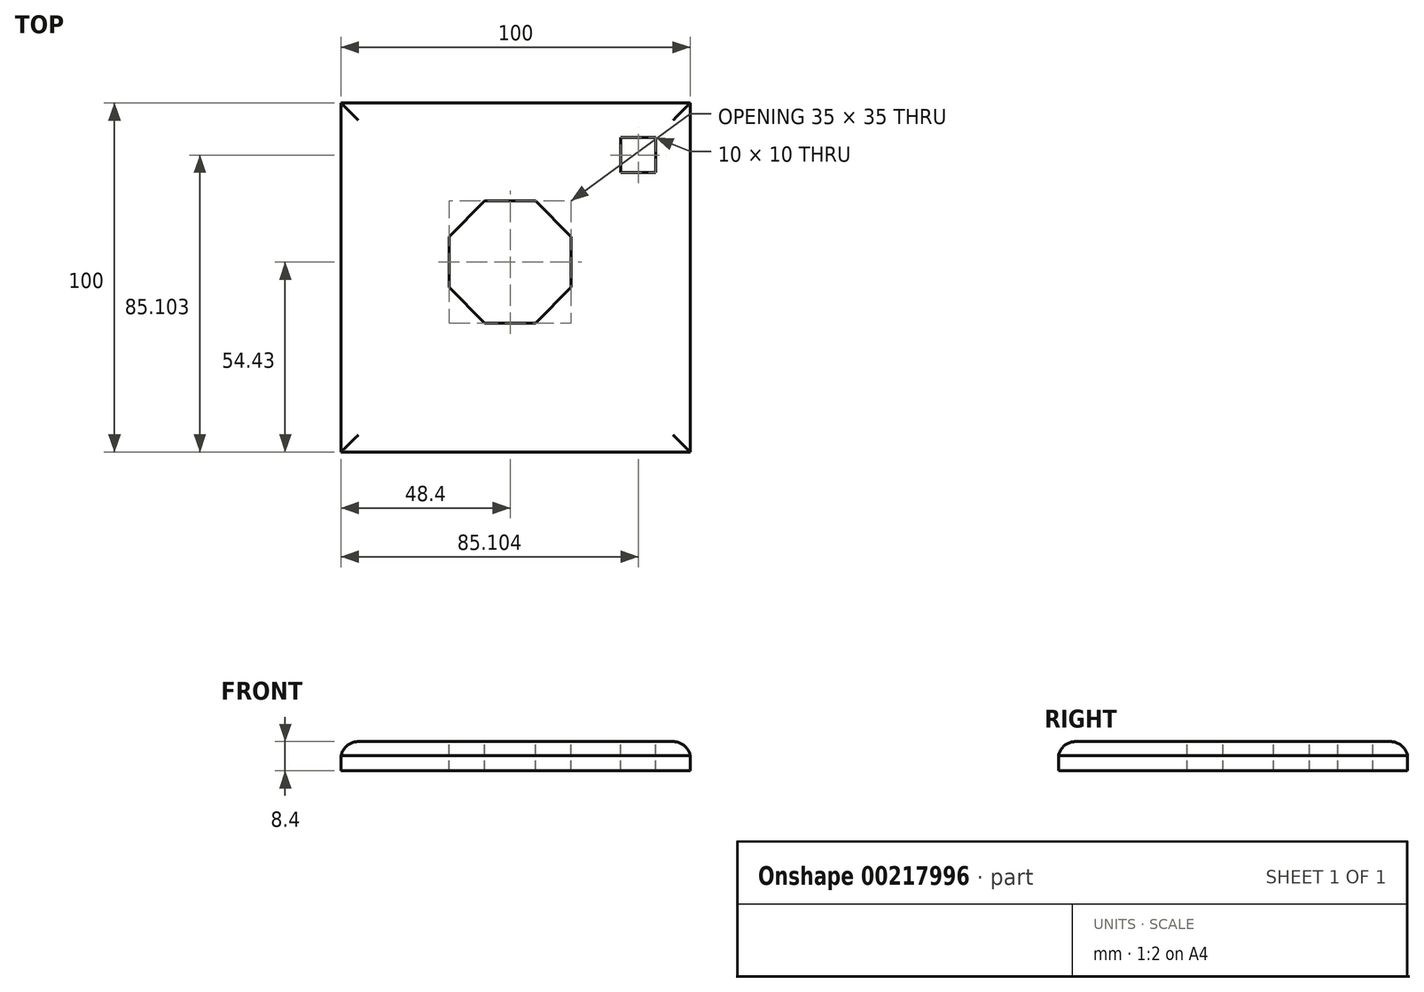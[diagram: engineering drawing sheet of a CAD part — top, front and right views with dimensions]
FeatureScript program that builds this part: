
annotation { "Feature Type Name" : "Feature", "Feature Type Description" : "" }
export const myFeature = defineFeature(function(context is Context, id is Id, definition is map)
    precondition{}
    {
        {
            var Q0;
            Q0=qCreatedBy(makeId("Top.planeOp"),FACE);
            var sketch = newSketch(context, id + "F0", { "sketchPlane" : qUnion([Q0])});
            skLineSegment(sketch, "E0.bottom", {"start": v(-48.4, 45.57) * mm, "end": v(51.6, 45.57) * mm});
            skLineSegment(sketch, "E0.top", {"start": v(-48.4, -54.43) * mm, "end": v(51.6, -54.43) * mm});
            skLineSegment(sketch, "E0.left", {"start": v(-48.4, 45.57) * mm, "end": v(-48.4, -54.43) * mm});
            skLineSegment(sketch, "E0.right", {"start": v(51.6, 45.57) * mm, "end": v(51.6, -54.43) * mm});
            skSolve(sketch);
        }
        {
            var Q0;
            Q0=makeQuery(id+"F0.imprint","IMPRINT",FACE,{"disambiguationData":[TD([[makeQuery(id+"F0.imprint","IMPRINT",EDGE,{"derivedFrom":sQuery(id+"F0.wireOp",EDGE,"E0.bottom")}),-1.0]])]});
            extrude(context, id + "F1", {"entities" : qUnion([Q0]), "depth" : 4 * mm});
        }
        {
            var Q0;
            Q0=makeQuery(id+"F1.opExtrude","CAP_FACE",FACE,{"disambiguationData":[OSD([sQuery(id+"F0.wireOp",EDGE,"E0.bottom"),sQuery(id+"F0.wireOp",EDGE,"E0.top"),sQuery(id+"F0.wireOp",EDGE,"E0.left"),sQuery(id+"F0.wireOp",EDGE,"E0.right")])],"isStart":false});
            var sketch = newSketch(context, id + "F2", { "sketchPlane" : qUnion([Q0])});
            skCircle(sketch, "E1.cCircle", {"center": v(0, 0) * mm, "radius": 17.5 * mm, "construction": true});
            skLineSegment(sketch, "E1.0", {"start": v(7.25, -17.5) * mm, "end": v(-7.25, -17.5) * mm});
            skLineSegment(sketch, "E1.1", {"start": v(-7.25, -17.5) * mm, "end": v(-17.5, -7.25) * mm});
            skLineSegment(sketch, "E1.2", {"start": v(-17.5, -7.25) * mm, "end": v(-17.5, 7.25) * mm});
            skLineSegment(sketch, "E1.3", {"start": v(-17.5, 7.25) * mm, "end": v(-7.25, 17.5) * mm});
            skLineSegment(sketch, "E1.4", {"start": v(-7.25, 17.5) * mm, "end": v(7.25, 17.5) * mm});
            skLineSegment(sketch, "E1.5", {"start": v(7.25, 17.5) * mm, "end": v(17.5, 7.25) * mm});
            skLineSegment(sketch, "E1.6", {"start": v(17.5, 7.25) * mm, "end": v(17.5, -7.25) * mm});
            skLineSegment(sketch, "E1.7", {"start": v(17.5, -7.25) * mm, "end": v(7.25, -17.5) * mm});
            skPoint(sketch, "E1.0.midPoint", {"position": v(0, -17.5) * mm});
            skSolve(sketch);
        }
        {
            var Q0;
            Q0=makeQuery(id+"F1.opExtrude","CAP_FACE",FACE,{"disambiguationData":[OSD([sQuery(id+"F0.wireOp",EDGE,"E0.bottom"),sQuery(id+"F0.wireOp",EDGE,"E0.top"),sQuery(id+"F0.wireOp",EDGE,"E0.left"),sQuery(id+"F0.wireOp",EDGE,"E0.right")])],"isStart":false});
            fillet(context, id + "F3", {"entities" : qUnion([Q0]), "radius" : 5 * mm, "tangentPropagation" : true, "allowEdgeOverflow" : false});
        }
        {
            var Q0;
            Q0=makeQuery(id+"F2.imprint","IMPRINT",FACE,{"disambiguationData":[TD([[makeQuery(id+"F2.imprint","IMPRINT",EDGE,{"derivedFrom":sQuery(id+"F2.wireOp",EDGE,"E1.0")}),1.0]])]});
            var sketch = newSketch(context, id + "F4", { "sketchPlane" : qUnion([Q0])});
            skLineSegment(sketch, "E2.bottom", {"start": v(41.7, 35.67) * mm, "end": v(31.7, 35.67) * mm});
            skLineSegment(sketch, "E2.top", {"start": v(41.7, 25.67) * mm, "end": v(31.7, 25.67) * mm});
            skLineSegment(sketch, "E2.left", {"start": v(41.7, 35.67) * mm, "end": v(41.7, 25.67) * mm});
            skLineSegment(sketch, "E2.right", {"start": v(31.7, 35.67) * mm, "end": v(31.7, 25.67) * mm});
            skSolve(sketch);
        }
        {
            var Q0;
            Q0=makeQuery(id+"F2.imprint","IMPRINT",FACE,{"disambiguationData":[TD([[makeQuery(id+"F2.imprint","IMPRINT",EDGE,{"derivedFrom":sQuery(id+"F2.wireOp",EDGE,"E1.0")}),-1.0]])]});
            extrude(context, id + "F5", {"entities" : qUnion([Q0]), "operationType" : NewBodyOperationType.REMOVE, "oppositeDirection" : true, "depth" : 25 * mm});
        }
        {
            var Q0;
            Q0=makeQuery(id+"F4.imprint","IMPRINT",FACE,{"disambiguationData":[TD([[makeQuery(id+"F4.imprint","IMPRINT",EDGE,{"derivedFrom":sQuery(id+"F4.wireOp",EDGE,"E2.bottom")}),1.0]])]});
            extrude(context, id + "F6", {"entities" : qUnion([Q0]), "operationType" : NewBodyOperationType.REMOVE, "oppositeDirection" : true, "depth" : 25 * mm});
        }
        {
            var Q0;
            Q0=makeQuery(id+"F1.opExtrude","CAP_FACE",FACE,{"disambiguationData":[OSD([sQuery(id+"F0.wireOp",EDGE,"E0.bottom"),sQuery(id+"F0.wireOp",EDGE,"E0.top"),sQuery(id+"F0.wireOp",EDGE,"E0.left"),sQuery(id+"F0.wireOp",EDGE,"E0.right")])],"isStart":true});
            extrude(context, id + "F7", {"entities" : qUnion([Q0]), "operationType" : NewBodyOperationType.ADD, "depth" : 4.4 * mm});
        }
    });
